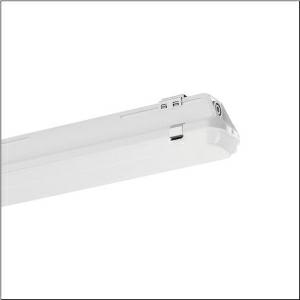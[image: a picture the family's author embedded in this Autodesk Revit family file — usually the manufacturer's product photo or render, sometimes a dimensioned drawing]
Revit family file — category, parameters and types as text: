
# Revit family: monsun_r__11_51fp10fp460l_0793
name_source: partatom
category: Lighting Fixtures
units: mm (PartAtom-declared; Revit-internal decimal feet)

## family parameters
Cut with Voids When Loaded = No
Host = Face
Light Source = No
Part Type = Normal
Room Calculation Point = No
Round Connector Dimension = Use Diameter
Shared = No

## types (1)
- --- (1 x LED, 6050 lm, 31.5 W, 4000K)
    Apparent Load = 32 VA
    CIE Flux Codes = 47 77 93 94 100
    Color Rendering = 80
    Color Temperature = 4000K
    Default Elevation = 1800 mm
    Description = Monsun® 11, damp-proof luminaire, chain hanger, primary optical cover: enclosure, of PMMA, light emission: direct distribution, primary light characteristic: symmetric, installation type: suspended mounting, surface-mounted, horizontal mounting, vertical mounting, LED, rated luminous flux: 6.050lm, luminous efficacy: 192lm/W, light colour: 840, colour temperature: 4000K, control gear: DALI 2, CLO, with terminal, 5-pole, max. 2.5mm², mains connection: 220..240V, AC, 50/60Hz, rated input power: 32W, luminaire housing, of glass-fibre reinforced polyester, uncoated, bright grey, incl. chain hanger, length: 1.590mm, width: 90mm, height: 88mm, clip for enclosure, of stainless steel (V2A), ceiling mounting element, of stainless steel (V2A), chain hanger, of stainless steel (V2A), protection rating (complete): IP66, insulation class (complete): insulation class I (protective earthing), certification: CE, ENEC, VDE, UKCA, protection symbol: D, impact resistance: IK04, permissible operating ambient temperature: -25..+40°C, standard: EN 50419, EN 60598-2-1, corresponds to IFS (International Featured Standards) requirements for safety and quality in the food industry, for indoor or canopied outdoor use, no direct snow, no direct sun, no direct rain, LABS conformity tested according to VDMA 24364:2018-05, contact your sales advisor before using the luminaires in applications with unclear chemical exposure, large temperature fluctuations or condensation-forming humidity, packaging unit: 1 piece
    Height = 89 mm
    Lamp = 1 x LED
    Lamp Light Flux = 6050 lm
    Lamp Power = 31.5 W
    Lamp count = 1
    Length = 1590 mm
    Luminous efficacy = 192 lm/W
    Manufacturer = Siteco
    ModVariant = No
    Model = 51FP10FP460L
    Mounting Place = Ceiling
    Mounting Type = Surface mounted
    Number of Poles = 1
    OnlyDefault = Yes
    Power Factor = 1
    Product Name = Monsun® 11
    Product group = damp-proof luminaire
    ProductGroupID = 301
    Protection Class = Protection class I
    Protection Degree = IP 66
    RLX_Detail_Level = 1
    RLX_Emergency_Light_Flux = 0 lm
    RLX_Emergency_Type = 0
    RLX_Emergency_Type_DB = No
    RlxData = <blob elided: 92349 chars, md5=fefb0967>
    Socket = socket
    Standby Power = 0 W
    System Light Flux = 6050 lm
    System Power = 32 W
    Type Comments = factory setting: luminous flux: 100 % | dim-lin: 254 | 219 mA
    Type Image = l_1349237.jpg
    URL = http://relux.com
    VarID = @adj_033671
    Voltage = 0 V
    Weight = 0.00 kg
    Width = 90 mm

## geometry (parser evidence)
native form markers: Blend x4, Sweep x12
no freeform markers — native parametric forms only
